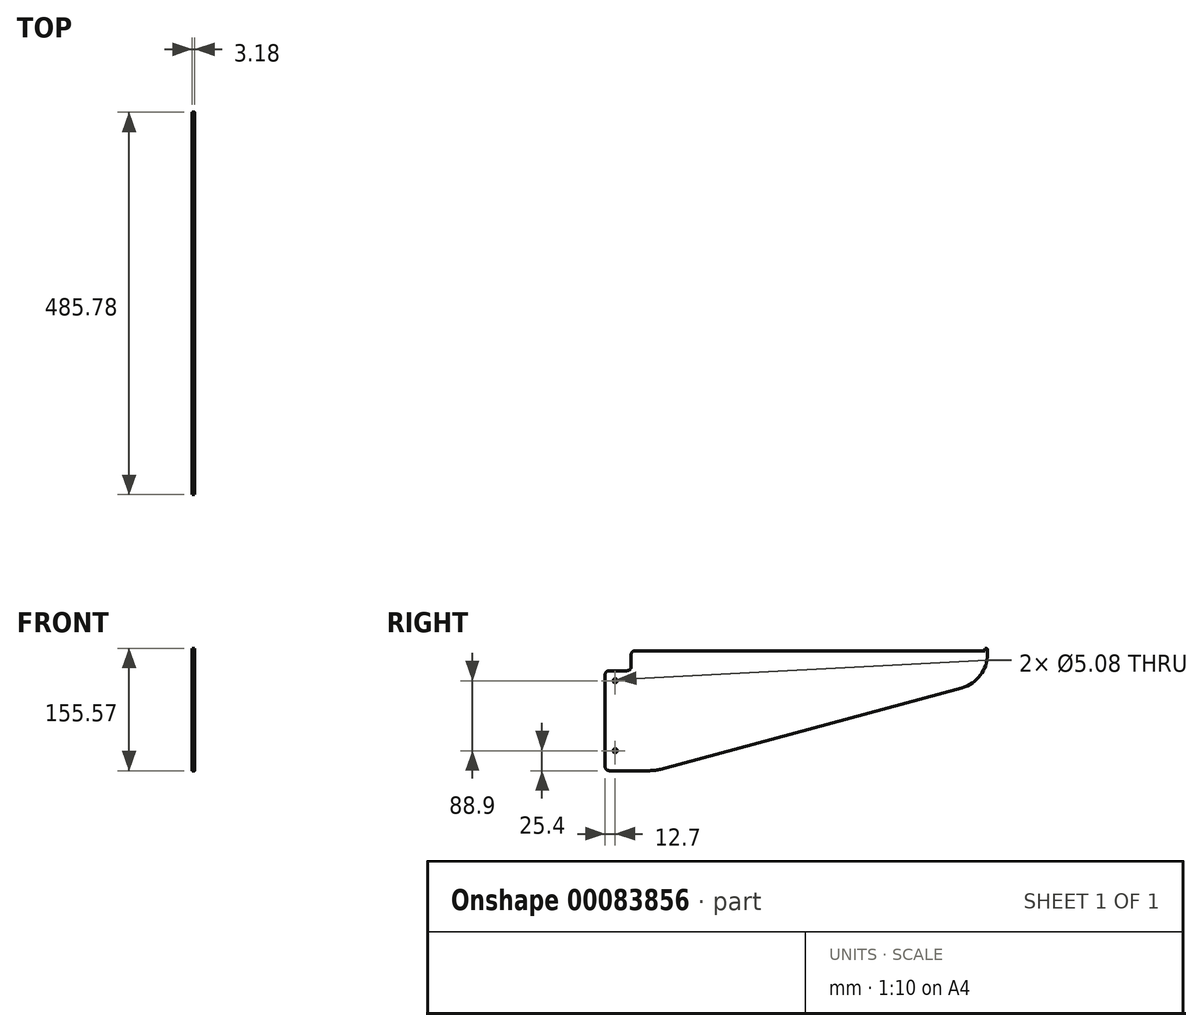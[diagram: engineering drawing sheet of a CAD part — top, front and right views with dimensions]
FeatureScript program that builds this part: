
annotation { "Feature Type Name" : "Feature", "Feature Type Description" : "" }
export const myFeature = defineFeature(function(context is Context, id is Id, definition is map)
    precondition{}
    {
        {
            var Q0;
            Q0=qCreatedBy(makeId("Right.planeOp"),FACE);
            var sketch = newSketch(context, id + "F0", { "sketchPlane" : qUnion([Q0])});
            skLineSegment(sketch, "E0", {"start": v(0, 0) * mm, "end": v(482.6, 0) * mm});
            skLineSegment(sketch, "E1", {"start": v(482.6, 0) * mm, "end": v(482.6, 3.18) * mm});
            skLineSegment(sketch, "E2", {"start": v(482.6, 3.18) * mm, "end": v(485.78, 3.18) * mm});
            skLineSegment(sketch, "E3", {"start": v(485.78, 3.18) * mm, "end": v(485.78, -38.1) * mm});
            skLineSegment(sketch, "E4", {"start": v(0, 0) * mm, "end": v(33.02, 0) * mm});
            skLineSegment(sketch, "E5", {"start": v(33.02, 0) * mm, "end": v(33.02, -25.4) * mm});
            skLineSegment(sketch, "E6", {"start": v(33.02, -25.4) * mm, "end": v(0, -25.4) * mm});
            skLineSegment(sketch, "E7", {"start": v(0, -25.4) * mm, "end": v(0, -152.4) * mm});
            skLineSegment(sketch, "E8", {"start": v(0, -152.4) * mm, "end": v(63.5, -152.4) * mm});
            skLineSegment(sketch, "E9", {"start": v(63.5, -152.4) * mm, "end": v(485.77, -38.1) * mm});
            skLineSegment(sketch, "E10", {"start": v(0, -25.4) * mm, "end": v(12.7, -25.4) * mm});
            skLineSegment(sketch, "E11", {"start": v(12.7, -25.4) * mm, "end": v(12.7, -38.1) * mm});
            skCircle(sketch, "E12", {"center": v(12.7, -38.1) * mm, "radius": 2.54 * mm});
            skCircle(sketch, "E13.0.1.0", {"center": v(12.7, -127) * mm, "radius": 2.54 * mm});
            skLineSegment(sketch, "E13.direction1", {"start": v(12.7, -38.1) * mm, "end": v(38.1, -38.1) * mm, "construction": true});
            skLineSegment(sketch, "E13.direction2", {"start": v(12.7, -38.1) * mm, "end": v(12.7, -127) * mm, "construction": true});
            skSolve(sketch);
        }
        {
            var Q0;
            Q0=makeQuery(id+"F0.imprint","IMPRINT",FACE,{"disambiguationData":[TD([[makeQuery(id+"F0.imprint","IMPRINT",EDGE,{"derivedFrom":sQuery(id+"F0.wireOp",EDGE,"E0")}),-1.0]])]});
            extrude(context, id + "F1", {"entities" : qUnion([Q0]), "depth" : 3.17 * mm});
        }
        {
            var Q0;
            Q0=makeQuery(id+"F1.opExtrude","SWEPT_EDGE",EDGE,{"disambiguationData":[OSD([sQuery(id+"F0.wireOp",EDGE,"E7"),sQuery(id+"F0.wireOp",EDGE,"E8")])]});
            var Q1;
            Q1=makeQuery(id+"F1.opExtrude","SWEPT_EDGE",EDGE,{"disambiguationData":[OSD([sQuery(id+"F0.wireOp",EDGE,"E7"),sQuery(id+"F0.wireOp",EDGE,"E10")])]});
            var Q2;
            Q2=makeQuery(id+"F1.opExtrude","SWEPT_EDGE",EDGE,{"disambiguationData":[OSD([sQuery(id+"F0.wireOp",EDGE,"E0"),sQuery(id+"F0.wireOp",EDGE,"E5")])]});
            var Q3;
            Q3=makeQuery(id+"F1.opExtrude","SWEPT_EDGE",EDGE,{"disambiguationData":[OSD([sQuery(id+"F0.wireOp",EDGE,"E5"),sQuery(id+"F0.wireOp",EDGE,"E6")])]});
            fillet(context, id + "F2", {"entities" : qUnion([Q0, Q1, Q2, Q3]), "radius" : 5.08 * mm, "tangentPropagation" : true, "allowEdgeOverflow" : false});
        }
        {
            var Q0;
            Q0=makeQuery(id+"F1.opExtrude","SWEPT_EDGE",EDGE,{"disambiguationData":[OSD([sQuery(id+"F0.wireOp",EDGE,"E2"),sQuery(id+"F0.wireOp",EDGE,"E3")])]});
            fillet(context, id + "F3", {"entities" : qUnion([Q0]), "radius" : 2.54 * mm, "tangentPropagation" : true, "allowEdgeOverflow" : false});
        }
        {
            var Q0;
            Q0=makeQuery(id+"F1.opExtrude","SWEPT_EDGE",EDGE,{"disambiguationData":[OSD([sQuery(id+"F0.wireOp",EDGE,"E3"),sQuery(id+"F0.wireOp",EDGE,"E9")])]});
            fillet(context, id + "F4", {"entities" : qUnion([Q0]), "radius" : 44.45 * mm, "tangentPropagation" : true, "allowEdgeOverflow" : false});
        }
        {
            var Q0;
            Q0=makeQuery(id+"F1.opExtrude","SWEPT_EDGE",EDGE,{"disambiguationData":[OSD([sQuery(id+"F0.wireOp",EDGE,"E8"),sQuery(id+"F0.wireOp",EDGE,"E9")])]});
            fillet(context, id + "F5", {"entities" : qUnion([Q0]), "radius" : 50.8 * mm, "tangentPropagation" : true, "allowEdgeOverflow" : false});
        }
    });
